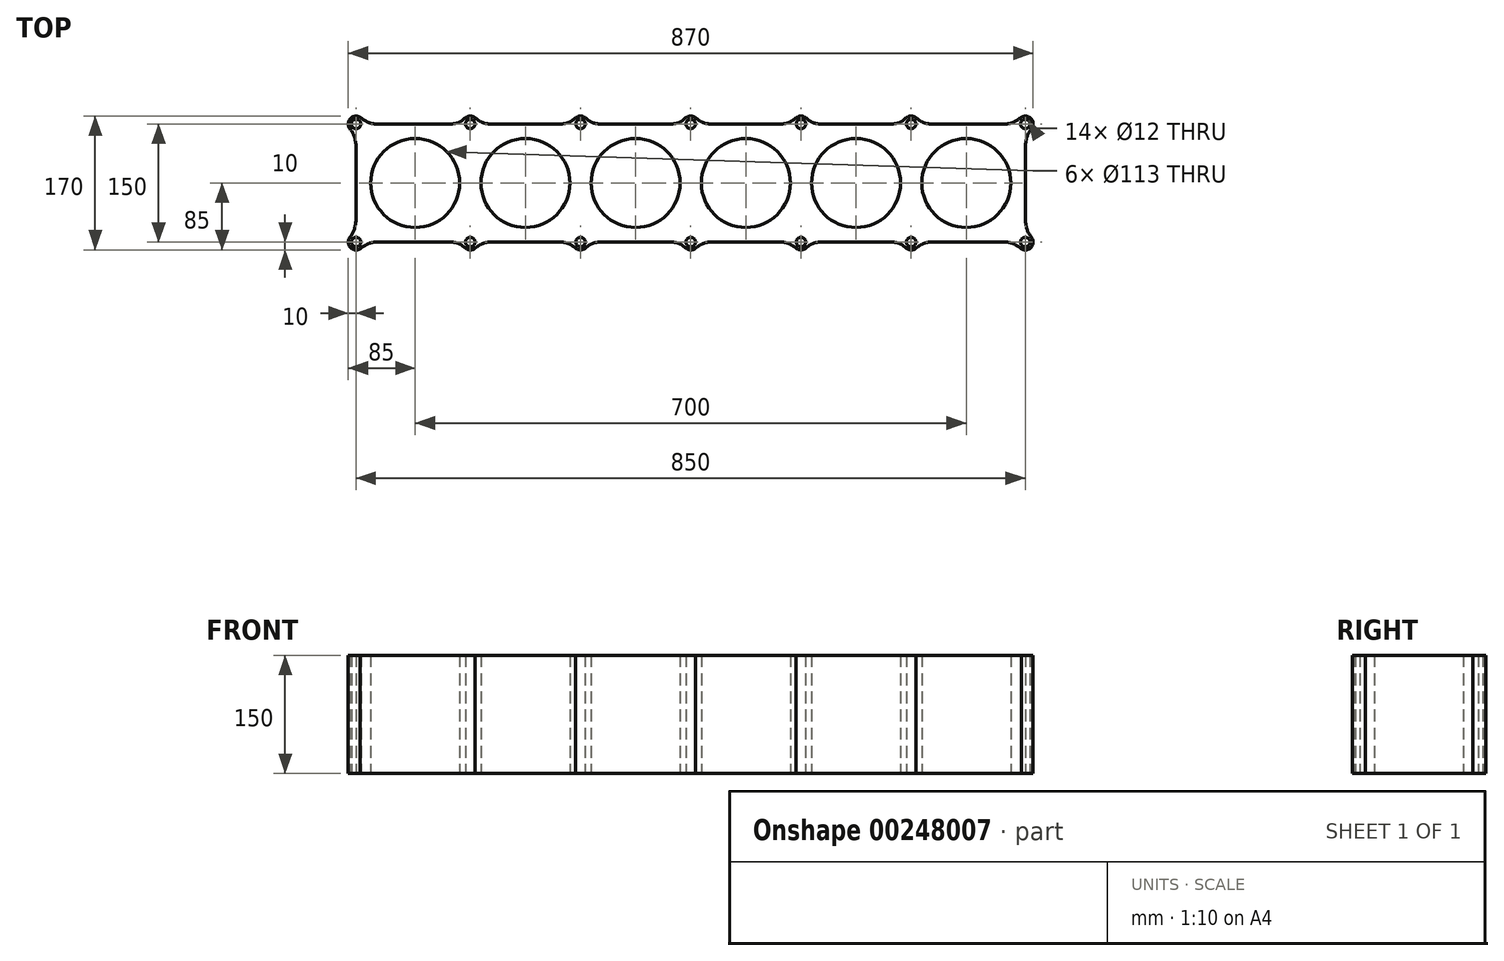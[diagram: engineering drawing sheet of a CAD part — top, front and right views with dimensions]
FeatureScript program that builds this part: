
annotation { "Feature Type Name" : "Feature", "Feature Type Description" : "" }
export const myFeature = defineFeature(function(context is Context, id is Id, definition is map)
    precondition{}
    {
        {
            var Q0;
            Q0=qCreatedBy(makeId("Top.planeOp"),FACE);
            var sketch = newSketch(context, id + "F0", { "sketchPlane" : qUnion([Q0])});
            skCircle(sketch, "E0", {"center": v(0, 0) * mm, "radius": 56.5 * mm});
            skLineSegment(sketch, "E1", {"start": v(0, 0) * mm, "end": v(762.28, 0) * mm, "construction": true});
            skLineSegment(sketch, "E2", {"start": v(70, -107.29) * mm, "end": v(70, 147.27) * mm, "construction": true});
            skCircle(sketch, "E3.MirrorC", {"center": v(140, 0) * mm, "radius": 56.5 * mm});
            skLineSegment(sketch, "E4", {"start": v(210, 153.73) * mm, "end": v(210, -144.18) * mm, "construction": true});
            skCircle(sketch, "E5.MirrorC", {"center": v(280, 0) * mm, "radius": 56.5 * mm});
            skLineSegment(sketch, "E6", {"start": v(350, 187.85) * mm, "end": v(350, -169.08) * mm, "construction": true});
            skCircle(sketch, "E7.MirrorC", {"center": v(420, 0) * mm, "radius": 56.5 * mm});
            skLineSegment(sketch, "E8", {"start": v(490, 152.8) * mm, "end": v(490, -133.11) * mm, "construction": true});
            skCircle(sketch, "E9.MirrorC", {"center": v(560, 0) * mm, "radius": 56.5 * mm});
            skLineSegment(sketch, "E10", {"start": v(630, 174.02) * mm, "end": v(630, -133.11) * mm, "construction": true});
            skCircle(sketch, "E11.MirrorC", {"center": v(700, 0) * mm, "radius": 56.5 * mm});
            skLineSegment(sketch, "E12.bottom", {"start": v(-45.28, 75) * mm, "end": v(44.38, 75) * mm});
            skLineSegment(sketch, "E12.top", {"start": v(-75, -75) * mm, "end": v(775, -75) * mm});
            skLineSegment(sketch, "E12.left", {"start": v(-75, 37.08) * mm, "end": v(-75, -75) * mm});
            skLineSegment(sketch, "E12.right", {"start": v(775, 75) * mm, "end": v(775, -75) * mm});
            skArc(sketch, "E13", {"start": v(-69.9, 83.6) * mm, "mid": v(-82.68, 81.4) * mm, "end": v(-82.54, 68.43) * mm});
            skFitSpline(sketch, "E14", {"points": [v(-82.54, 68.43) * mm, v(-75, 37.08) * mm], "startDerivative": vector(22.63, -28.22) * mm, "endDerivative": vector(0, -34.03) * mm});
            skFitSpline(sketch, "E15", {"points": [v(-69.9, 83.6) * mm, v(-45.28, 75) * mm], "startDerivative": vector(32.01, -25.8) * mm, "endDerivative": vector(27.67, 0) * mm});
            skCircle(sketch, "E16", {"center": v(-75, 75) * mm, "radius": 6 * mm});
            skArc(sketch, "E17", {"start": v(76.2, 82.85) * mm, "mid": v(69.5, 84.99) * mm, "end": v(63.04, 82.18) * mm});
            skFitSpline(sketch, "E18", {"points": [v(44.38, 75) * mm, v(63.04, 82.18) * mm], "startDerivative": vector(24.1, 0) * mm, "endDerivative": vector(15.07, 14.63) * mm});
            skFitSpline(sketch, "E19", {"points": [v(76.2, 82.85) * mm, v(96.41, 75) * mm], "startDerivative": vector(16.74, -14.7) * mm, "endDerivative": vector(26.96, 0) * mm});
            skCircle(sketch, "E20", {"center": v(70, 75) * mm, "radius": 6 * mm});
            skLineSegment(sketch, "E21.trimOffspring", {"start": v(96.41, 75) * mm, "end": v(140, 75) * mm});
            skLineSegment(sketch, "E22", {"start": v(140, 0) * mm, "end": v(140, 108.6) * mm, "construction": true});
            skCircle(sketch, "E23.MirrorC", {"center": v(210, 75) * mm, "radius": 6 * mm});
            skFitSpline(sketch, "E24.MirrorCS", {"points": [v(203.8, 82.85) * mm, v(183.59, 75) * mm], "startDerivative": vector(-16.74, -14.7) * mm, "endDerivative": vector(-26.96, 0) * mm});
            skArc(sketch, "E25.MirrorCS", {"start": v(203.8, 82.85) * mm, "mid": v(210.5, 84.99) * mm, "end": v(216.96, 82.18) * mm});
            skFitSpline(sketch, "E26.MirrorCS", {"points": [v(235.62, 75) * mm, v(216.96, 82.18) * mm], "startDerivative": vector(-24.1, 0) * mm, "endDerivative": vector(-15.07, 14.63) * mm});
            skLineSegment(sketch, "E27", {"start": v(280, 0) * mm, "end": v(280, 102.6) * mm, "construction": true});
            skFitSpline(sketch, "E28.MirrorCS", {"points": [v(324.38, 75) * mm, v(343.04, 82.18) * mm], "startDerivative": vector(24.1, 0) * mm, "endDerivative": vector(15.07, 14.63) * mm});
            skArc(sketch, "E29.MirrorCS", {"start": v(356.2, 82.85) * mm, "mid": v(349.5, 84.99) * mm, "end": v(343.04, 82.18) * mm});
            skFitSpline(sketch, "E30.MirrorCS", {"points": [v(356.2, 82.85) * mm, v(376.41, 75) * mm], "startDerivative": vector(16.74, -14.7) * mm, "endDerivative": vector(26.96, 0) * mm});
            skCircle(sketch, "E31.MirrorC", {"center": v(350, 75) * mm, "radius": 6 * mm});
            skLineSegment(sketch, "E32", {"start": v(420, 0) * mm, "end": v(420, 118.63) * mm, "construction": true});
            skFitSpline(sketch, "E33.MirrorCS", {"points": [v(483.8, 82.85) * mm, v(463.59, 75) * mm], "startDerivative": vector(-16.74, -14.7) * mm, "endDerivative": vector(-26.96, 0) * mm});
            skArc(sketch, "E34.MirrorCS", {"start": v(483.8, 82.85) * mm, "mid": v(490.5, 84.99) * mm, "end": v(496.96, 82.18) * mm});
            skFitSpline(sketch, "E35.MirrorCS", {"points": [v(515.62, 75) * mm, v(496.96, 82.18) * mm], "startDerivative": vector(-24.1, 0) * mm, "endDerivative": vector(-15.07, 14.63) * mm});
            skCircle(sketch, "E36.MirrorC", {"center": v(490, 75) * mm, "radius": 6 * mm});
            skLineSegment(sketch, "E37", {"start": v(560, 0) * mm, "end": v(560, 102.94) * mm, "construction": true});
            skCircle(sketch, "E38.MirrorC", {"center": v(630, 75) * mm, "radius": 6 * mm});
            skFitSpline(sketch, "E39.MirrorCS", {"points": [v(604.38, 75) * mm, v(623.04, 82.18) * mm], "startDerivative": vector(24.1, 0) * mm, "endDerivative": vector(15.07, 14.63) * mm});
            skLineSegment(sketch, "E40.MirrorCS", {"start": v(630, 152.8) * mm, "end": v(630, -133.11) * mm, "construction": true});
            skArc(sketch, "E41.MirrorCS", {"start": v(636.2, 82.85) * mm, "mid": v(629.5, 84.99) * mm, "end": v(623.04, 82.18) * mm});
            skFitSpline(sketch, "E42.MirrorCS", {"points": [v(636.2, 82.85) * mm, v(656.41, 75) * mm], "startDerivative": vector(16.74, -14.7) * mm, "endDerivative": vector(26.96, 0) * mm});
            skFitSpline(sketch, "E43.MirrorCS", {"points": [v(782.54, 68.43) * mm, v(775, 37.08) * mm], "startDerivative": vector(-22.63, -28.22) * mm, "endDerivative": vector(0, -34.03) * mm});
            skArc(sketch, "E44.MirrorCS", {"start": v(769.9, 83.6) * mm, "mid": v(782.68, 81.4) * mm, "end": v(782.54, 68.43) * mm});
            skCircle(sketch, "E45.MirrorC", {"center": v(775, 75) * mm, "radius": 6 * mm});
            skFitSpline(sketch, "E46.MirrorCS", {"points": [v(769.9, 83.6) * mm, v(745.28, 75) * mm], "startDerivative": vector(-32.01, -25.8) * mm, "endDerivative": vector(-27.67, 0) * mm});
            skFitSpline(sketch, "E47.MirrorCS", {"points": [v(-82.54, -68.43) * mm, v(-75, -37.08) * mm], "startDerivative": vector(22.63, 28.22) * mm, "endDerivative": vector(0, 34.03) * mm});
            skArc(sketch, "E48.MirrorCS", {"start": v(-69.9, -83.6) * mm, "mid": v(-82.68, -81.4) * mm, "end": v(-82.54, -68.43) * mm});
            skFitSpline(sketch, "E49.MirrorCS", {"points": [v(-69.9, -83.6) * mm, v(-45.28, -75) * mm], "startDerivative": vector(32.01, 25.8) * mm, "endDerivative": vector(27.67, 0) * mm});
            skFitSpline(sketch, "E50.MirrorCS", {"points": [v(44.38, -75) * mm, v(63.04, -82.18) * mm], "startDerivative": vector(24.1, 0) * mm, "endDerivative": vector(15.07, -14.63) * mm});
            skArc(sketch, "E51.MirrorCS", {"start": v(76.2, -82.85) * mm, "mid": v(69.5, -84.99) * mm, "end": v(63.04, -82.18) * mm});
            skFitSpline(sketch, "E52.MirrorCS", {"points": [v(76.2, -82.85) * mm, v(96.41, -75) * mm], "startDerivative": vector(16.74, 14.7) * mm, "endDerivative": vector(26.96, 0) * mm});
            skFitSpline(sketch, "E53.MirrorCS", {"points": [v(203.8, -82.85) * mm, v(183.59, -75) * mm], "startDerivative": vector(-16.74, 14.7) * mm, "endDerivative": vector(-26.96, 0) * mm});
            skArc(sketch, "E54.MirrorCS", {"start": v(203.8, -82.85) * mm, "mid": v(210.5, -84.99) * mm, "end": v(216.96, -82.18) * mm});
            skFitSpline(sketch, "E55.MirrorCS", {"points": [v(235.62, -75) * mm, v(216.96, -82.18) * mm], "startDerivative": vector(-24.1, 0) * mm, "endDerivative": vector(-15.07, -14.63) * mm});
            skFitSpline(sketch, "E56.MirrorCS", {"points": [v(324.38, -75) * mm, v(343.04, -82.18) * mm], "startDerivative": vector(24.1, 0) * mm, "endDerivative": vector(15.07, -14.63) * mm});
            skArc(sketch, "E57.MirrorCS", {"start": v(356.2, -82.85) * mm, "mid": v(349.5, -84.99) * mm, "end": v(343.04, -82.18) * mm});
            skCircle(sketch, "E58.MirrorC", {"center": v(350, -75) * mm, "radius": 6 * mm});
            skFitSpline(sketch, "E59.MirrorCS", {"points": [v(356.2, -82.85) * mm, v(376.41, -75) * mm], "startDerivative": vector(16.74, 14.7) * mm, "endDerivative": vector(26.96, 0) * mm});
            skFitSpline(sketch, "E60.MirrorCS", {"points": [v(483.8, -82.85) * mm, v(463.59, -75) * mm], "startDerivative": vector(-16.74, 14.7) * mm, "endDerivative": vector(-26.96, 0) * mm});
            skArc(sketch, "E61.MirrorCS", {"start": v(483.8, -82.85) * mm, "mid": v(490.5, -84.99) * mm, "end": v(496.96, -82.18) * mm});
            skCircle(sketch, "E62.MirrorC", {"center": v(490, -75) * mm, "radius": 6 * mm});
            skFitSpline(sketch, "E63.MirrorCS", {"points": [v(515.62, -75) * mm, v(496.96, -82.18) * mm], "startDerivative": vector(-24.1, 0) * mm, "endDerivative": vector(-15.07, -14.63) * mm});
            skFitSpline(sketch, "E64.MirrorCS", {"points": [v(604.38, -75) * mm, v(623.04, -82.18) * mm], "startDerivative": vector(24.1, 0) * mm, "endDerivative": vector(15.07, -14.63) * mm});
            skArc(sketch, "E65.MirrorCS", {"start": v(636.2, -82.85) * mm, "mid": v(629.5, -84.99) * mm, "end": v(623.04, -82.18) * mm});
            skCircle(sketch, "E66.MirrorC", {"center": v(630, -75) * mm, "radius": 6 * mm});
            skFitSpline(sketch, "E67.MirrorCS", {"points": [v(636.2, -82.85) * mm, v(656.41, -75) * mm], "startDerivative": vector(16.74, 14.7) * mm, "endDerivative": vector(26.96, 0) * mm});
            skFitSpline(sketch, "E68.MirrorCS", {"points": [v(769.9, -83.6) * mm, v(745.28, -75) * mm], "startDerivative": vector(-32.01, 25.8) * mm, "endDerivative": vector(-27.67, 0) * mm});
            skArc(sketch, "E69.MirrorCS", {"start": v(769.9, -83.6) * mm, "mid": v(782.68, -81.4) * mm, "end": v(782.54, -68.43) * mm});
            skCircle(sketch, "E70.MirrorC", {"center": v(775, -75) * mm, "radius": 6 * mm});
            skFitSpline(sketch, "E71.MirrorCS", {"points": [v(782.54, -68.43) * mm, v(775, -37.08) * mm], "startDerivative": vector(-22.63, 28.22) * mm, "endDerivative": vector(0, 34.03) * mm});
            skCircle(sketch, "E72.MirrorC", {"center": v(210, -75) * mm, "radius": 6 * mm});
            skCircle(sketch, "E73.MirrorC", {"center": v(70, -75) * mm, "radius": 6 * mm});
            skCircle(sketch, "E74.MirrorC", {"center": v(-75, -75) * mm, "radius": 6 * mm});
            skLineSegment(sketch, "E75.trimOffspring", {"start": v(235.62, 75) * mm, "end": v(324.38, 75) * mm});
            skLineSegment(sketch, "E76", {"start": v(140, 75) * mm, "end": v(183.59, 75) * mm});
            skLineSegment(sketch, "E77.trimOffspring", {"start": v(376.41, 75) * mm, "end": v(463.59, 75) * mm});
            skLineSegment(sketch, "E78.trimOffspring", {"start": v(515.62, 75) * mm, "end": v(560, 75) * mm});
            skLineSegment(sketch, "E79.trimOffspring", {"start": v(656.41, 75) * mm, "end": v(745.28, 75) * mm});
            skLineSegment(sketch, "E80.trimOffspring", {"start": v(769, 75) * mm, "end": v(775, 75) * mm});
            skLineSegment(sketch, "E81", {"start": v(769, 75) * mm, "end": v(745.28, 75) * mm});
            skLineSegment(sketch, "E82", {"start": v(-45.28, 75) * mm, "end": v(-69, 75) * mm});
            skLineSegment(sketch, "E83", {"start": v(-75.15, 69) * mm, "end": v(-75, 37.08) * mm});
            skLineSegment(sketch, "E84", {"start": v(44.38, 75) * mm, "end": v(96.41, 75) * mm});
            skLineSegment(sketch, "E85", {"start": v(183.59, 75) * mm, "end": v(235.62, 75) * mm});
            skLineSegment(sketch, "E86", {"start": v(324.38, 75) * mm, "end": v(376.41, 75) * mm});
            skLineSegment(sketch, "E87", {"start": v(463.59, 75) * mm, "end": v(515.62, 75) * mm});
            skLineSegment(sketch, "E88", {"start": v(560, 75) * mm, "end": v(604.38, 75) * mm});
            skSolve(sketch);
        }
        {
            var Q0;
            Q0 = qSketchRegion(id + "F0", true);
            extrude(context, id + "F1", {"entities" : qUnion([Q0]), "depth" : 150 * mm});
        }
    });
